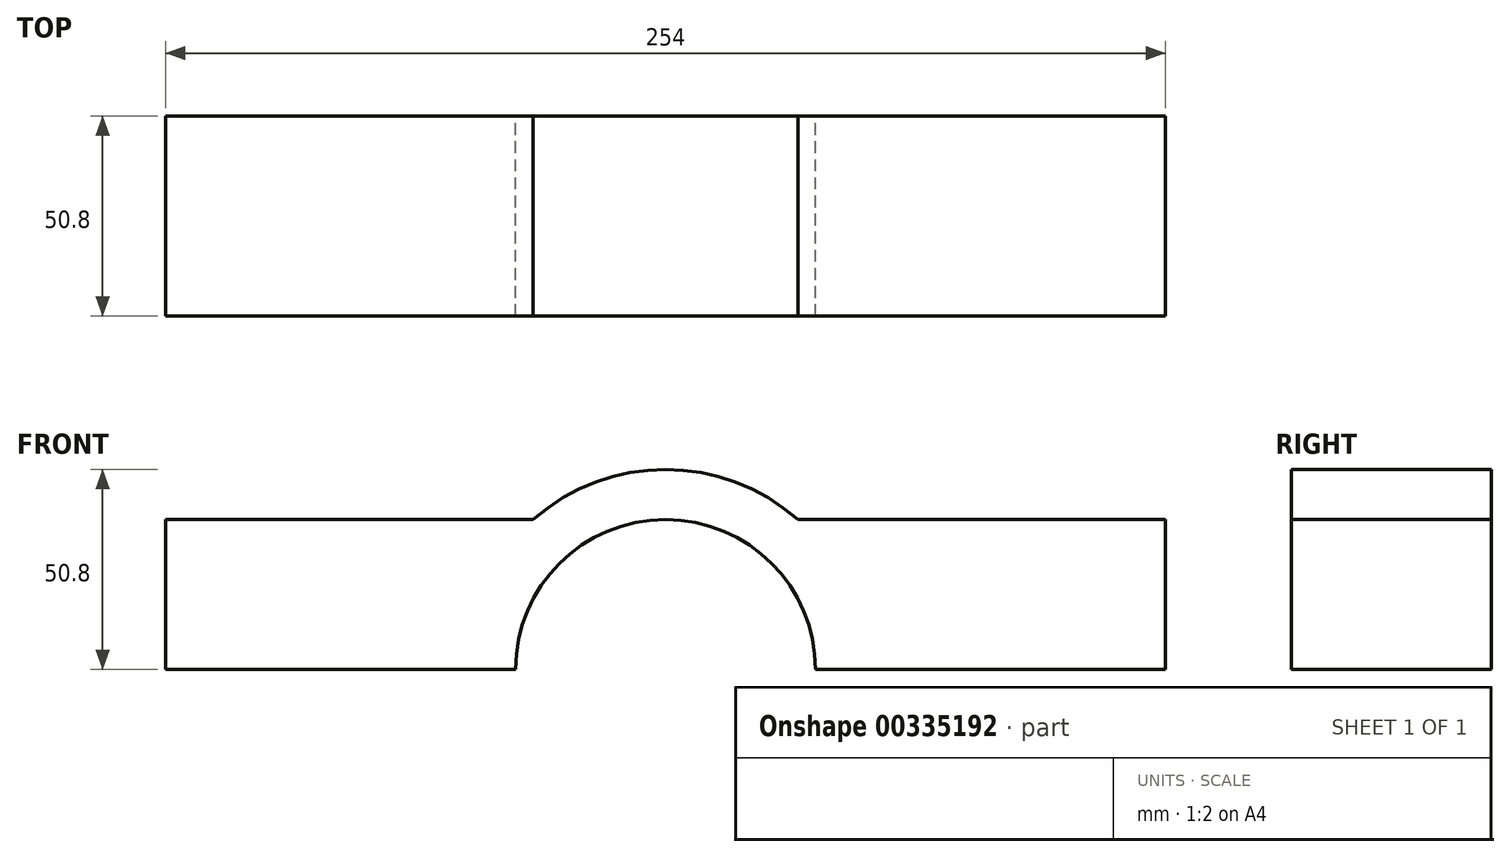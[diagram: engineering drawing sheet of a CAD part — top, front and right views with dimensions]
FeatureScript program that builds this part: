
annotation { "Feature Type Name" : "Feature", "Feature Type Description" : "" }
export const myFeature = defineFeature(function(context is Context, id is Id, definition is map)
    precondition{}
    {
        {
            var Q0;
            Q0=qCreatedBy(makeId("Front.planeOp"),FACE);
            var sketch = newSketch(context, id + "F0", { "sketchPlane" : qUnion([Q0])});
            skLineSegment(sketch, "E0.top", {"start": v(-127, -38.1) * mm, "end": v(127, -38.1) * mm});
            skLineSegment(sketch, "E0.left", {"start": v(-127, 38.1) * mm, "end": v(-127, -38.1) * mm});
            skLineSegment(sketch, "E0.right", {"start": v(127, 38.1) * mm, "end": v(127, -38.1) * mm});
            skPoint(sketch, "E0.middle", {"position": v(0, 0) * mm});
            skLineSegment(sketch, "E1", {"start": v(0, 12.7) * mm, "end": v(0, -38.1) * mm, "construction": true});
            skArc(sketch, "E2", {"start": v(38.1, -38.1) * mm, "mid": v(0, 0) * mm, "end": v(-38.1, -38.1) * mm});
            skArc(sketch, "E3", {"start": v(50.8, -38.1) * mm, "mid": v(0, 12.7) * mm, "end": v(-50.8, -38.1) * mm});
            skLineSegment(sketch, "E4", {"start": v(-33.6, 0) * mm, "end": v(-127, 0) * mm});
            skLineSegment(sketch, "E5", {"start": v(33.6, 0) * mm, "end": v(127, 0) * mm});
            skLineSegment(sketch, "E6", {"start": v(-127, 38.1) * mm, "end": v(127, 38.1) * mm});
            skSolve(sketch);
        }
        {
            var Q0;
            {var subQ5=sQuery(id+"F0.wireOp",EDGE,"E4");Q0=makeQuery(id+"F0.imprint","IMPRINT",FACE,{"disambiguationData":[TD([[makeQuery(id+"F0.imprint","IMPRINT",EDGE,{"derivedFrom":subQ5}),1.0]])]});}
            var Q1;
            {var subQ5=sQuery(id+"F0.wireOp",EDGE,"E5");Q1=makeQuery(id+"F0.imprint","IMPRINT",FACE,{"disambiguationData":[TD([[makeQuery(id+"F0.imprint","IMPRINT",EDGE,{"derivedFrom":subQ5}),-1.0]])]});}
            var Q2;
            {var subQ4=sQuery(id+"F0.wireOp",EDGE,"E2");Q2=makeQuery(id+"F0.imprint","IMPRINT",FACE,{"disambiguationData":[TD([[makeQuery(id+"F0.imprint","IMPRINT",EDGE,{"derivedFrom":subQ4}),-1.0]])]});}
            extrude(context, id + "F1", {"entities" : qUnion([Q0, Q1, Q2]), "depth" : 50.8 * mm});
        }
    });
